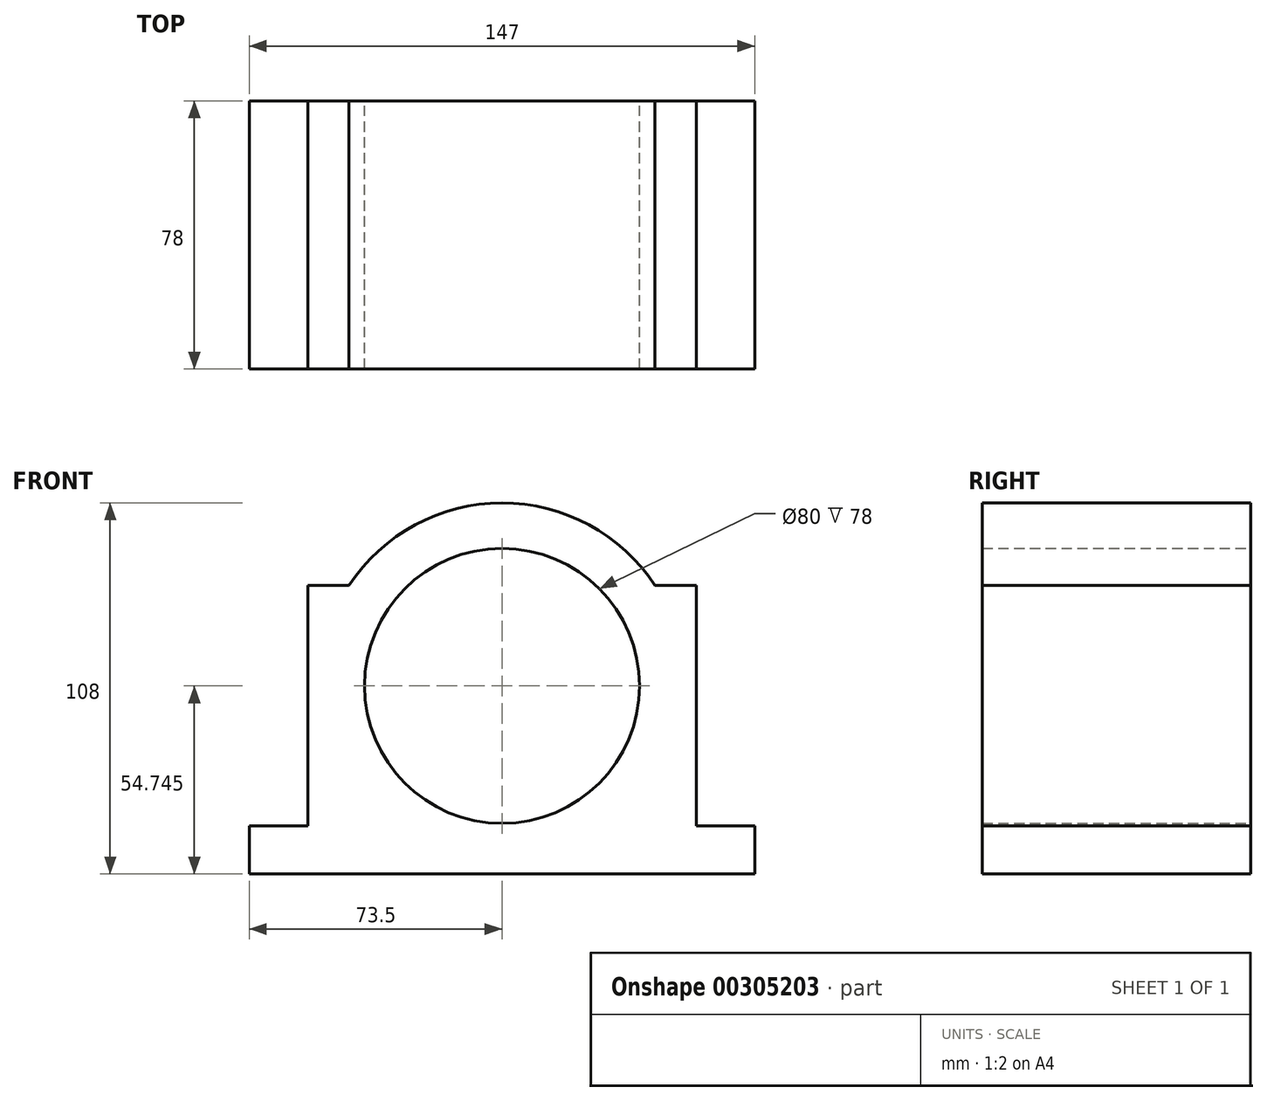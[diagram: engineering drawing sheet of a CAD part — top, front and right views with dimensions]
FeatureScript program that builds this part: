
annotation { "Feature Type Name" : "Feature", "Feature Type Description" : "" }
export const myFeature = defineFeature(function(context is Context, id is Id, definition is map)
    precondition{}
    {
        {
            var Q0;
            Q0=qCreatedBy(makeId("Front.planeOp"),FACE);
            var sketch = newSketch(context, id + "F0", { "sketchPlane" : qUnion([Q0])});
            skLineSegment(sketch, "E0", {"start": v(0, 0) * mm, "end": v(-147, 0) * mm});
            skLineSegment(sketch, "E1", {"start": v(-147, 0) * mm, "end": v(-147, 14) * mm});
            skLineSegment(sketch, "E2", {"start": v(-147, 14) * mm, "end": v(-130, 14) * mm});
            skLineSegment(sketch, "E3", {"start": v(-130, 14) * mm, "end": v(-130, 84) * mm});
            skLineSegment(sketch, "E4", {"start": v(-130, 84) * mm, "end": v(-118, 84) * mm});
            skLineSegment(sketch, "E5", {"start": v(0, 0) * mm, "end": v(0, 14) * mm});
            skLineSegment(sketch, "E6", {"start": v(0, 14) * mm, "end": v(-17, 14) * mm});
            skLineSegment(sketch, "E7", {"start": v(-17, 14) * mm, "end": v(-17, 84) * mm});
            skLineSegment(sketch, "E8", {"start": v(-17, 84) * mm, "end": v(-29, 84) * mm});
            skPoint(sketch, "E9.endSnap0", {"position": v(-73.5, 0) * mm});
            skArc(sketch, "E10", {"start": v(-29, 84) * mm, "mid": v(-73.5, 108) * mm, "end": v(-118, 84) * mm});
            skCircle(sketch, "E11", {"center": v(-73.5, 54.74) * mm, "radius": 40 * mm});
            skSolve(sketch);
        }
        {
            var Q0;
            Q0=makeQuery(id+"F0.imprint","IMPRINT",FACE,{"disambiguationData":[TD([[makeQuery(id+"F0.imprint","IMPRINT",EDGE,{"derivedFrom":sQuery(id+"F0.wireOp",EDGE,"E0")}),-1.0]])]});
            extrude(context, id + "F1", {"entities" : qUnion([Q0]), "depth" : 78 * mm});
        }
    });
